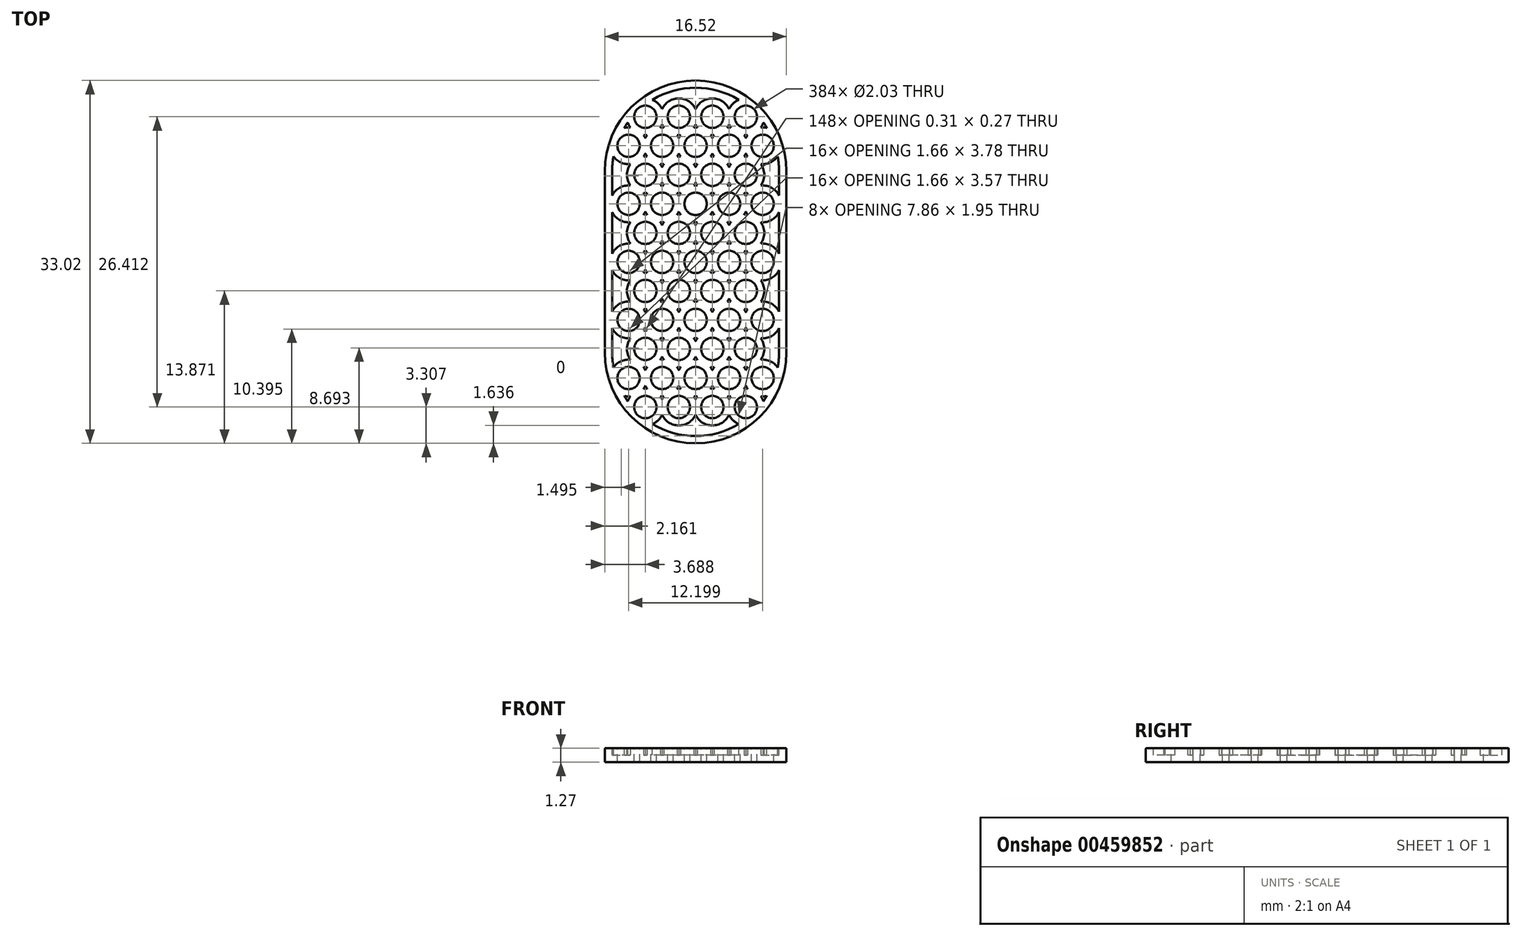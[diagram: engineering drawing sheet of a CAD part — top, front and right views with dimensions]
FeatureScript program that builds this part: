
annotation { "Feature Type Name" : "Feature", "Feature Type Description" : "" }
export const myFeature = defineFeature(function(context is Context, id is Id, definition is map)
    precondition{}
    {
        {
            var Q0;
            Q0=qCreatedBy(makeId("Top.planeOp"),FACE);
            var sketch = newSketch(context, id + "F0", { "sketchPlane" : qUnion([Q0])});
            skCircle(sketch, "E0", {"center": v(0, -13.21) * mm, "radius": 8.26 * mm});
            skCircle(sketch, "E1", {"center": v(0, -29.72) * mm, "radius": 8.26 * mm});
            skLineSegment(sketch, "E2", {"start": v(8.26, -13.21) * mm, "end": v(8.26, -29.72) * mm});
            skLineSegment(sketch, "E3", {"start": v(-8.26, -13.21) * mm, "end": v(-8.26, -29.72) * mm});
            skSolve(sketch);
        }
        {
            var Q0;
            Q0 = qSketchRegion(id + "F0", true);
            extrude(context, id + "F1", {"entities" : qUnion([Q0]), "depth" : 1.27 * mm});
        }
        {
            var Q0;
            Q0=makeQuery(id+"F1.opExtrude","CAP_FACE",FACE,{"disambiguationData":[OSD([sQuery(id+"F0.wireOp",EDGE,"E0"),sQuery(id+"F0.wireOp",EDGE,"E1"),sQuery(id+"F0.wireOp",EDGE,"E2"),sQuery(id+"F0.wireOp",EDGE,"E3")])],"isStart":false});
            fillet(context, id + "F2", {"entities" : qUnion([Q0]), "radius" : 0.05 * mm, "tangentPropagation" : true, "allowEdgeOverflow" : false});
        }
        {
            var Q0;
            Q0=makeQuery(id+"F1.opExtrude","CAP_FACE",FACE,{"disambiguationData":[OSD([sQuery(id+"F0.wireOp",EDGE,"E0"),sQuery(id+"F0.wireOp",EDGE,"E1"),sQuery(id+"F0.wireOp",EDGE,"E2"),sQuery(id+"F0.wireOp",EDGE,"E3")])],"isStart":false});
            var sketch = newSketch(context, id + "F3", { "sketchPlane" : qUnion([Q0])});
            skCircle(sketch, "E4", {"center": v(0, -21.47) * mm, "radius": 1.02 * mm});
            skPoint(sketch, "E4.centerSnap0", {"position": v(-8.2, -21.47) * mm});
            skCircle(sketch, "E5", {"center": v(3.05, -21.47) * mm, "radius": 1.02 * mm});
            skLineSegment(sketch, "E6", {"start": v(0, -21.47) * mm, "end": v(1.52, -18.83) * mm, "construction": true});
            skLineSegment(sketch, "E7", {"start": v(1.52, -18.83) * mm, "end": v(3.05, -21.47) * mm, "construction": true});
            skLineSegment(sketch, "E8", {"start": v(0, -21.47) * mm, "end": v(3.05, -21.47) * mm, "construction": true});
            skCircle(sketch, "E9", {"center": v(1.52, -18.83) * mm, "radius": 1.02 * mm});
            skLineSegment(sketch, "E10", {"start": v(1.52, -18.83) * mm, "end": v(4.57, -18.83) * mm, "construction": true});
            skLineSegment(sketch, "E11", {"start": v(4.57, -18.83) * mm, "end": v(3.05, -21.47) * mm, "construction": true});
            skCircle(sketch, "E12", {"center": v(4.57, -18.83) * mm, "radius": 1.02 * mm});
            skLineSegment(sketch, "E13", {"start": v(1.52, -18.83) * mm, "end": v(0, -16.19) * mm, "construction": true});
            skLineSegment(sketch, "E14", {"start": v(1.52, -18.83) * mm, "end": v(-1.52, -18.83) * mm, "construction": true});
            skLineSegment(sketch, "E15", {"start": v(-1.52, -18.83) * mm, "end": v(0, -16.19) * mm, "construction": true});
            skCircle(sketch, "E16", {"center": v(0, -16.19) * mm, "radius": 1.02 * mm});
            skCircle(sketch, "E17.0.1.0", {"center": v(0, -16.18) * mm, "radius": 1.02 * mm});
            skCircle(sketch, "E17.0.1.1", {"center": v(3.05, -16.18) * mm, "radius": 1.02 * mm});
            skCircle(sketch, "E17.0.1.2", {"center": v(1.52, -13.54) * mm, "radius": 1.02 * mm});
            skCircle(sketch, "E17.0.1.3", {"center": v(4.57, -13.54) * mm, "radius": 1.02 * mm});
            skCircle(sketch, "E17.0.2.0", {"center": v(0, -10.9) * mm, "radius": 1.02 * mm});
            skCircle(sketch, "E17.0.2.1", {"center": v(3.05, -10.9) * mm, "radius": 1.02 * mm});
            skCircle(sketch, "E17.0.2.2", {"center": v(1.52, -8.26) * mm, "radius": 1.02 * mm});
            skCircle(sketch, "E17.0.2.3", {"center": v(4.57, -8.26) * mm, "radius": 1.02 * mm});
            skLineSegment(sketch, "E17.direction1", {"start": v(0, -21.47) * mm, "end": v(25.4, -21.47) * mm, "construction": true});
            skLineSegment(sketch, "E17.direction2", {"start": v(0, -21.47) * mm, "end": v(0, -16.18) * mm, "construction": true});
            skLineSegment(sketch, "E18", {"start": v(4.57, -13.54) * mm, "end": v(3.05, -10.9) * mm, "construction": true});
            skLineSegment(sketch, "E19", {"start": v(3.05, -10.9) * mm, "end": v(6.1, -10.9) * mm, "construction": true});
            skLineSegment(sketch, "E20", {"start": v(6.1, -10.9) * mm, "end": v(4.57, -13.54) * mm, "construction": true});
            skCircle(sketch, "E21", {"center": v(6.1, -10.9) * mm, "radius": 1.02 * mm});
            skLineSegment(sketch, "E22", {"start": v(4.57, -13.54) * mm, "end": v(6.1, -16.18) * mm, "construction": true});
            skLineSegment(sketch, "E23", {"start": v(6.1, -16.18) * mm, "end": v(3.05, -16.18) * mm, "construction": true});
            skLineSegment(sketch, "E24", {"start": v(3.05, -16.18) * mm, "end": v(4.57, -13.54) * mm, "construction": true});
            skCircle(sketch, "E25", {"center": v(6.1, -16.18) * mm, "radius": 1.02 * mm});
            skLineSegment(sketch, "E26", {"start": v(3.05, -21.47) * mm, "end": v(6.1, -21.47) * mm, "construction": true});
            skLineSegment(sketch, "E27", {"start": v(6.1, -21.47) * mm, "end": v(4.57, -18.83) * mm, "construction": true});
            skCircle(sketch, "E28", {"center": v(6.1, -21.47) * mm, "radius": 1.02 * mm});
            skLineSegment(sketch, "E29", {"start": v(-8.2, -21.47) * mm, "end": v(10.53, -21.47) * mm, "construction": true});
            skLineSegment(sketch, "E30", {"start": v(0, -5) * mm, "end": v(0, -37.93) * mm, "construction": true});
            skCircle(sketch, "E31.MirrorC", {"center": v(-1.52, -8.26) * mm, "radius": 1.02 * mm});
            skCircle(sketch, "E32.MirrorC", {"center": v(-4.57, -8.26) * mm, "radius": 1.02 * mm});
            skLineSegment(sketch, "E33.MirrorCS", {"start": v(-3.05, -10.9) * mm, "end": v(-6.1, -10.9) * mm, "construction": true});
            skCircle(sketch, "E34.MirrorC", {"center": v(-6.1, -10.9) * mm, "radius": 1.02 * mm});
            skCircle(sketch, "E35.MirrorC", {"center": v(-3.05, -10.9) * mm, "radius": 1.02 * mm});
            skCircle(sketch, "E36.MirrorC", {"center": v(-1.52, -13.54) * mm, "radius": 1.02 * mm});
            skCircle(sketch, "E37.MirrorC", {"center": v(-4.57, -13.54) * mm, "radius": 1.02 * mm});
            skCircle(sketch, "E38.MirrorC", {"center": v(-6.1, -16.18) * mm, "radius": 1.02 * mm});
            skCircle(sketch, "E39.MirrorC", {"center": v(-3.05, -16.18) * mm, "radius": 1.02 * mm});
            skCircle(sketch, "E40.MirrorC", {"center": v(-1.52, -18.83) * mm, "radius": 1.02 * mm});
            skCircle(sketch, "E41.MirrorC", {"center": v(-4.57, -18.83) * mm, "radius": 1.02 * mm});
            skCircle(sketch, "E42.MirrorC", {"center": v(-3.05, -21.47) * mm, "radius": 1.02 * mm});
            skCircle(sketch, "E43.MirrorC", {"center": v(-6.1, -21.47) * mm, "radius": 1.02 * mm});
            skCircle(sketch, "E44.MirrorC", {"center": v(4.57, -24.1) * mm, "radius": 1.02 * mm});
            skCircle(sketch, "E45.MirrorC", {"center": v(1.52, -24.1) * mm, "radius": 1.02 * mm});
            skCircle(sketch, "E46.MirrorC", {"center": v(-1.52, -24.1) * mm, "radius": 1.02 * mm});
            skCircle(sketch, "E47.MirrorC", {"center": v(-4.57, -24.1) * mm, "radius": 1.02 * mm});
            skCircle(sketch, "E48.MirrorC", {"center": v(-6.1, -26.75) * mm, "radius": 1.02 * mm});
            skCircle(sketch, "E49.MirrorC", {"center": v(-3.05, -26.75) * mm, "radius": 1.02 * mm});
            skCircle(sketch, "E50.MirrorC", {"center": v(0, -26.75) * mm, "radius": 1.02 * mm});
            skCircle(sketch, "E51.MirrorC", {"center": v(3.05, -26.75) * mm, "radius": 1.02 * mm});
            skCircle(sketch, "E52.MirrorC", {"center": v(6.1, -26.75) * mm, "radius": 1.02 * mm});
            skCircle(sketch, "E53.MirrorC", {"center": v(4.57, -29.39) * mm, "radius": 1.02 * mm});
            skCircle(sketch, "E54.MirrorC", {"center": v(1.52, -29.39) * mm, "radius": 1.02 * mm});
            skCircle(sketch, "E55.MirrorC", {"center": v(-1.52, -29.39) * mm, "radius": 1.02 * mm});
            skCircle(sketch, "E56.MirrorC", {"center": v(-4.57, -29.39) * mm, "radius": 1.02 * mm});
            skCircle(sketch, "E57.MirrorC", {"center": v(-6.1, -32.03) * mm, "radius": 1.02 * mm});
            skCircle(sketch, "E58.MirrorC", {"center": v(-3.05, -32.03) * mm, "radius": 1.02 * mm});
            skCircle(sketch, "E59.MirrorC", {"center": v(0, -32.03) * mm, "radius": 1.02 * mm});
            skCircle(sketch, "E60.MirrorC", {"center": v(3.05, -32.03) * mm, "radius": 1.02 * mm});
            skCircle(sketch, "E61.MirrorC", {"center": v(6.1, -32.03) * mm, "radius": 1.02 * mm});
            skCircle(sketch, "E62.MirrorC", {"center": v(4.57, -34.67) * mm, "radius": 1.02 * mm});
            skCircle(sketch, "E63.MirrorC", {"center": v(1.52, -34.67) * mm, "radius": 1.02 * mm});
            skCircle(sketch, "E64.MirrorC", {"center": v(-1.52, -34.67) * mm, "radius": 1.02 * mm});
            skCircle(sketch, "E65.MirrorC", {"center": v(-4.57, -34.67) * mm, "radius": 1.02 * mm});
            skSolve(sketch);
        }
        {
            var Q0;
            Q0 = qSketchRegion(id + "F3", true);
            extrude(context, id + "F4", {"entities" : qUnion([Q0]), "operationType" : NewBodyOperationType.REMOVE, "endBound" : BoundingType.THROUGH_ALL, "oppositeDirection" : true, "depth" : 25.4 * mm});
        }
        {
            var Q0;
            Q0=makeQuery(id+"F1.opExtrude","CAP_FACE",FACE,{"disambiguationData":[OSD([sQuery(id+"F0.wireOp",EDGE,"E0"),sQuery(id+"F0.wireOp",EDGE,"E1"),sQuery(id+"F0.wireOp",EDGE,"E2"),sQuery(id+"F0.wireOp",EDGE,"E3")])],"isStart":false});
            shell(context, id + "F5", {"entities" : qUnion([Q0]), "thickness" : 0.66 * mm});
        }
    });
